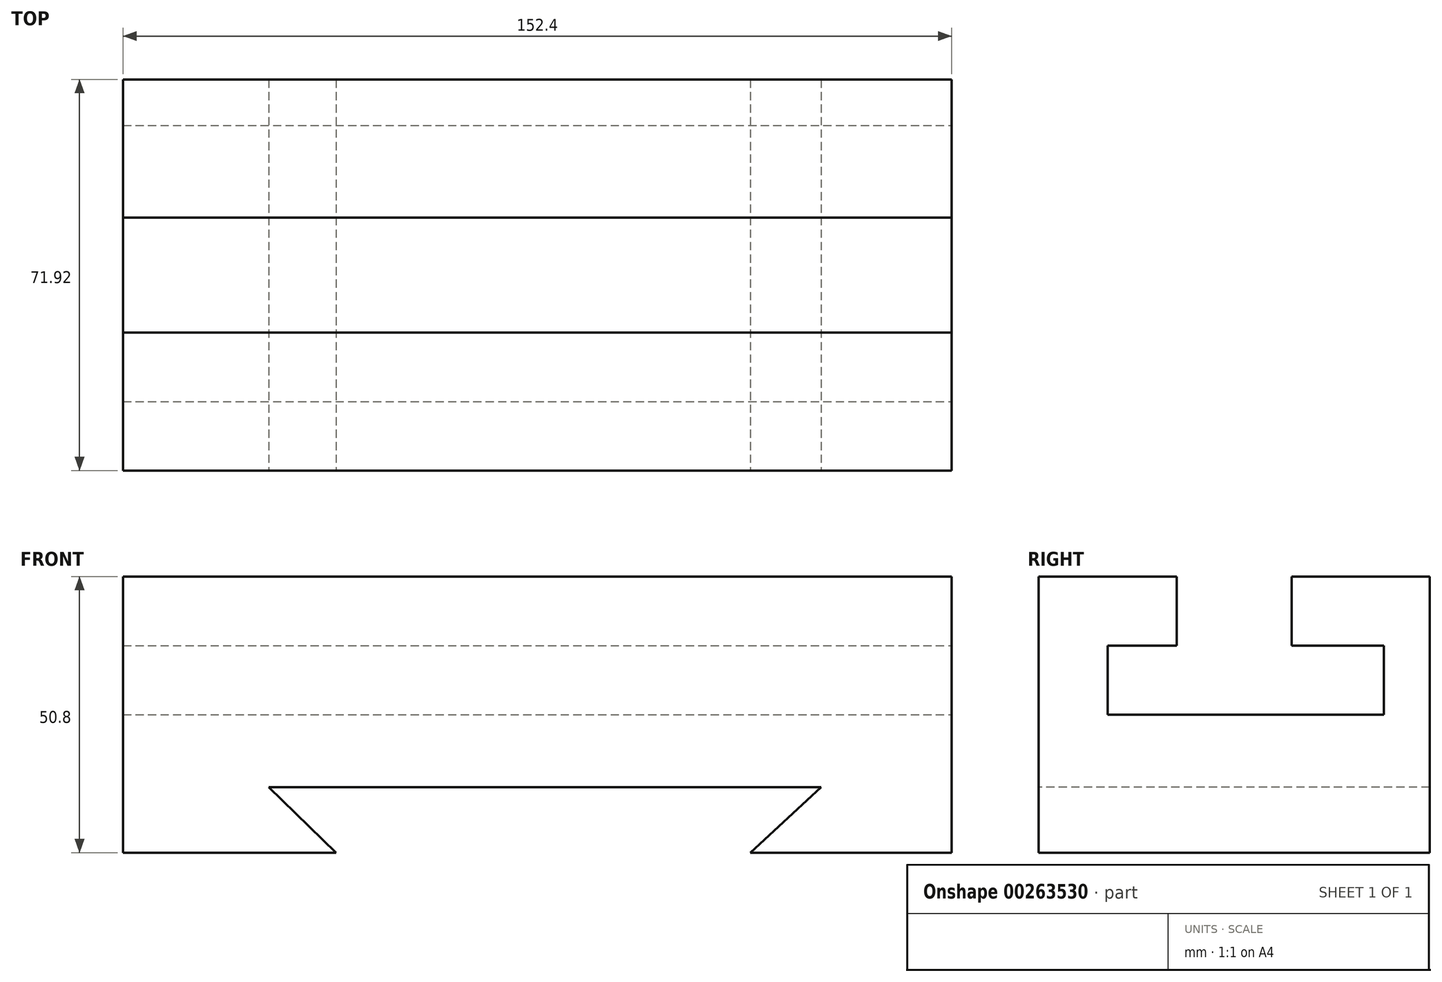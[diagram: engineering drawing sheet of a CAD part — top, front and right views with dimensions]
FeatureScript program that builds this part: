
annotation { "Feature Type Name" : "Feature", "Feature Type Description" : "" }
export const myFeature = defineFeature(function(context is Context, id is Id, definition is map)
    precondition{}
    {
        {
            var Q0;
            Q0=qCreatedBy(makeId("Right.planeOp"),FACE);
            var sketch = newSketch(context, id + "F0", { "sketchPlane" : qUnion([Q0])});
            skLineSegment(sketch, "E0.bottom", {"start": v(-34.07, 38.74) * mm, "end": v(-8.67, 38.74) * mm});
            skLineSegment(sketch, "E0.top", {"start": v(-34.07, -12.06) * mm, "end": v(37.85, -12.06) * mm});
            skLineSegment(sketch, "E0.left", {"start": v(-34.07, 38.74) * mm, "end": v(-34.07, -12.06) * mm});
            skLineSegment(sketch, "E0.right", {"start": v(37.85, 38.74) * mm, "end": v(37.85, -12.06) * mm});
            skLineSegment(sketch, "E1", {"start": v(-8.67, 38.74) * mm, "end": v(-8.67, 26.04) * mm});
            skLineSegment(sketch, "E2", {"start": v(-8.67, 26.04) * mm, "end": v(-21.37, 26.04) * mm});
            skLineSegment(sketch, "E3", {"start": v(-21.37, 26.04) * mm, "end": v(-21.37, 13.34) * mm});
            skLineSegment(sketch, "E4", {"start": v(-21.37, 13.34) * mm, "end": v(29.43, 13.34) * mm});
            skLineSegment(sketch, "E5", {"start": v(29.43, 13.34) * mm, "end": v(29.43, 26.04) * mm});
            skLineSegment(sketch, "E6", {"start": v(29.43, 26.04) * mm, "end": v(12.45, 26.04) * mm});
            skLineSegment(sketch, "E7", {"start": v(12.45, 26.04) * mm, "end": v(12.45, 38.74) * mm});
            skLineSegment(sketch, "E8.trimOffspring", {"start": v(12.45, 38.74) * mm, "end": v(37.85, 38.74) * mm});
            skSolve(sketch);
        }
        {
            var Q0;
            Q0 = qSketchRegion(id + "F0", true);
            extrude(context, id + "F1", {"entities" : qUnion([Q0]), "oppositeDirection" : true, "depth" : 152.4 * mm});
        }
        {
            var Q0;
            Q0 = qSketchRegion(id + "F0", true);
            extrude(context, id + "F2", {"entities" : qUnion([Q0]), "operationType" : NewBodyOperationType.ADD, "oppositeDirection" : true, "depth" : 152.4 * mm});
        }
        {
            var Q0;
            Q0=makeQuery(id+"F1.opExtrude","SWEPT_FACE",FACE,{"disambiguationData":[OSD([sQuery(id+"F0.wireOp",EDGE,"E0.left")])]});
            var sketch = newSketch(context, id + "F3", { "sketchPlane" : qUnion([Q0])});
            skLineSegment(sketch, "E9", {"start": v(-113.22, -12.06) * mm, "end": v(-37.02, -12.06) * mm});
            skLineSegment(sketch, "E10", {"start": v(-24, 0) * mm, "end": v(-125.6, 0) * mm});
            skLineSegment(sketch, "E11", {"start": v(-125.6, 0) * mm, "end": v(-113.22, -12.06) * mm});
            skLineSegment(sketch, "E12", {"start": v(-24, 0) * mm, "end": v(-37.02, -12.06) * mm});
            skSolve(sketch);
        }
        {
            var Q0;
            Q0=makeQuery(id+"F3.imprint","IMPRINT",FACE,{"disambiguationData":[TD([[makeQuery(id+"F3.imprint","IMPRINT",EDGE,{"derivedFrom":sQuery(id+"F3.wireOp",EDGE,"E9")}),1.0]])]});
            extrude(context, id + "F4", {"entities" : qUnion([Q0]), "operationType" : NewBodyOperationType.REMOVE, "oppositeDirection" : true, "depth" : 76.2 * mm});
        }
    });
